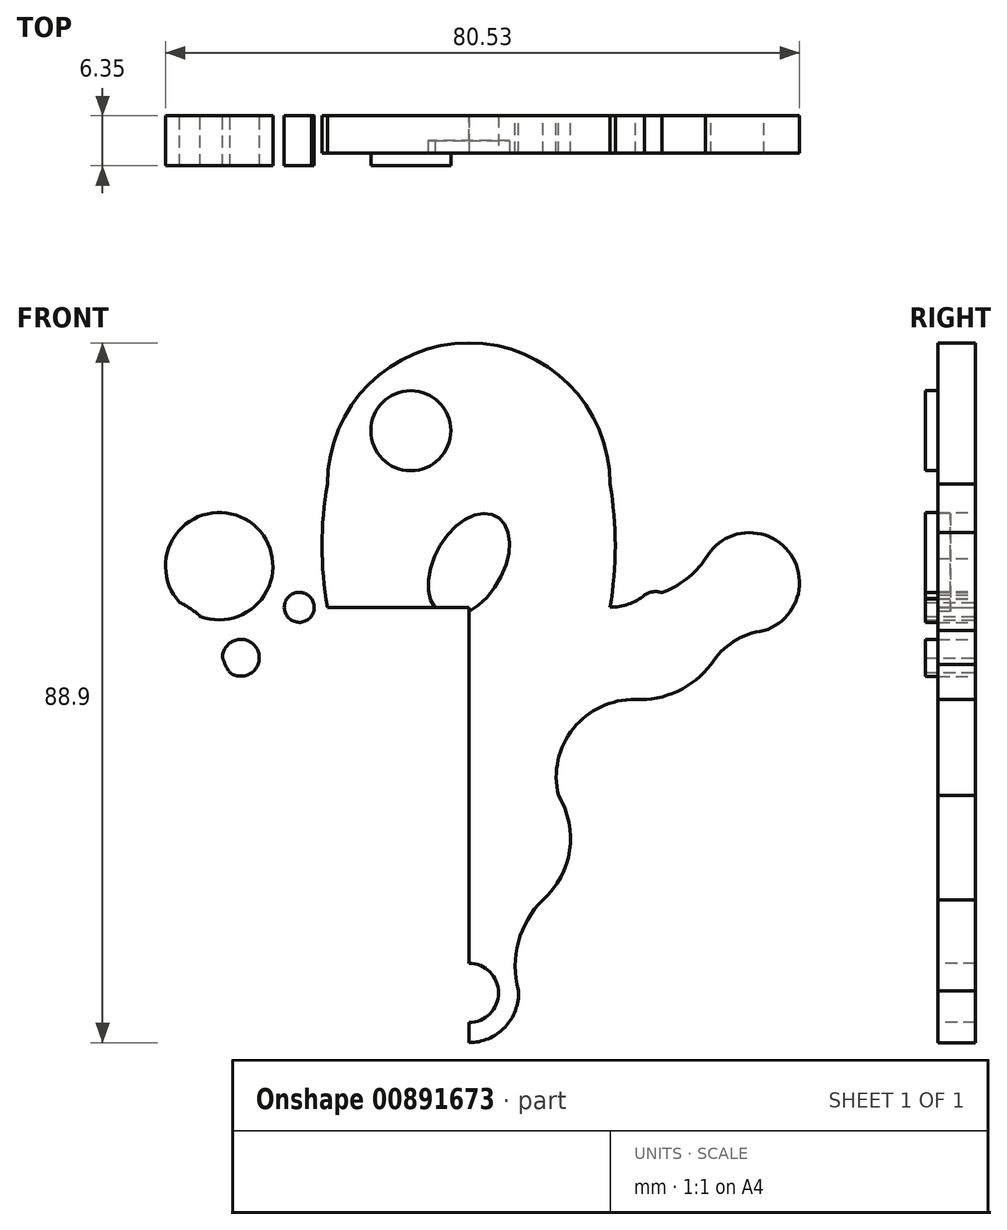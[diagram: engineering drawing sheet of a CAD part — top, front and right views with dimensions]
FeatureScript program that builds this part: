
annotation { "Feature Type Name" : "Feature", "Feature Type Description" : "" }
export const myFeature = defineFeature(function(context is Context, id is Id, definition is map)
    precondition{}
    {
        {
            var Q0;
            Q0=qCreatedBy(makeId("Front.planeOp"),FACE);
            var sketch = newSketch(context, id + "F0", { "sketchPlane" : qUnion([Q0])});
            skLineSegment(sketch, "E0.bottom", {"start": v(-17.94, 11.59) * mm, "end": v(17.94, 11.59) * mm});
            skLineSegment(sketch, "E0.top", {"start": v(-17.94, 27.23) * mm, "end": v(17.94, 27.23) * mm});
            skPoint(sketch, "E0.middle", {"position": v(0, 19.41) * mm});
            skArc(sketch, "E1", {"start": v(17.94, 27.23) * mm, "mid": v(0, 45.18) * mm, "end": v(-17.94, 27.23) * mm});
            skLineSegment(sketch, "E2", {"start": v(-17.94, 11.59) * mm, "end": v(0, 11.59) * mm});
            skLineSegment(sketch, "E3", {"start": v(0, 11.59) * mm, "end": v(0, -27.44) * mm});
            skLineSegment(sketch, "E4", {"start": v(0, -27.44) * mm, "end": v(0, -34) * mm});
            skCircle(sketch, "E5", {"center": v(-31.7, 16.82) * mm, "radius": 6.82 * mm});
            skCircle(sketch, "E6", {"center": v(35.65, 14.71) * mm, "radius": 6.36 * mm});
            skCircle(sketch, "E7", {"center": v(0, -37.4) * mm, "radius": 6.33 * mm});
            skCircle(sketch, "E8", {"center": v(-28.95, 5.17) * mm, "radius": 2.34 * mm});
            skCircle(sketch, "E9", {"center": v(-21.53, 11.59) * mm, "radius": 1.9 * mm});
            skArc(sketch, "E10", {"start": v(-19.98, 12.7) * mm, "mid": v(-19.1, 11.88) * mm, "end": v(-17.94, 11.59) * mm});
            skArc(sketch, "E11", {"start": v(-25.07, 18.4) * mm, "mid": v(-23.74, 15.74) * mm, "end": v(-21.82, 13.47) * mm});
            skArc(sketch, "E12", {"start": v(-6.2, -36.14) * mm, "mid": v(-8.21, -28.4) * mm, "end": v(-14.49, -23.44) * mm});
            skArc(sketch, "E13", {"start": v(-31.29, 5.17) * mm, "mid": v(-29.02, 1.8) * mm, "end": v(-25.38, 0) * mm});
            skPoint(sketch, "E14.startSnap0", {"position": v(10.2, -17.56) * mm});
            skArc(sketch, "E15", {"start": v(21.15, -0.12) * mm, "mid": v(13.28, -3.81) * mm, "end": v(11.38, -12.3) * mm});
            skArc(sketch, "E16", {"start": v(21.15, -0.12) * mm, "mid": v(26.51, 0.92) * mm, "end": v(30.77, 4.35) * mm});
            skCircle(sketch, "E17", {"center": v(23.71, 11.2) * mm, "radius": 2.37 * mm});
            skArc(sketch, "E18", {"start": v(24.52, 13.44) * mm, "mid": v(27.64, 15.17) * mm, "end": v(30.08, 17.78) * mm});
            skArc(sketch, "E19", {"start": v(17.94, 11.59) * mm, "mid": v(20.27, 11.99) * mm, "end": v(22.33, 13.14) * mm});
            skArc(sketch, "E20", {"start": v(37.47, 8.62) * mm, "mid": v(33.64, 7.23) * mm, "end": v(30.77, 4.35) * mm});
            skArc(sketch, "E21", {"start": v(-17.94, 27.23) * mm, "mid": v(-18.64, 19.41) * mm, "end": v(-17.94, 11.59) * mm});
            skArc(sketch, "E22", {"start": v(17.94, 11.59) * mm, "mid": v(18.6, 19.41) * mm, "end": v(17.94, 27.23) * mm});
            skArc(sketch, "E23", {"start": v(-20.49, -14.03) * mm, "mid": v(-19.15, -19.8) * mm, "end": v(-14.49, -23.44) * mm});
            skArc(sketch, "E24", {"start": v(-20.49, -14.03) * mm, "mid": v(-19.5, -5.82) * mm, "end": v(-25.38, 0) * mm});
            skArc(sketch, "E25", {"start": v(-31.29, 5.17) * mm, "mid": v(-33.14, 9.34) * mm, "end": v(-36.7, 12.19) * mm});
            skArc(sketch, "E26", {"start": v(9.44, -25.57) * mm, "mid": v(12.8, -19.28) * mm, "end": v(11.38, -12.3) * mm});
            skArc(sketch, "E27", {"start": v(9.44, -25.57) * mm, "mid": v(6.3, -30.92) * mm, "end": v(6.33, -37.12) * mm});
            skLineSegment(sketch, "E28", {"start": v(0, 45.18) * mm, "end": v(0, -43.72) * mm});
            skSolve(sketch);
        }
        {
            var Q0;
            Q0=makeQuery(id+"F0.imprint","IMPRINT",FACE,{"disambiguationData":[TD([[makeQuery(id+"F0.imprint","IMPRINT",EDGE,{"derivedFrom":sQuery(id+"F0.wireOp",EDGE,"E0.top")}),1.0]])]});
            var Q1;
            Q1=makeQuery(id+"F0.imprint","IMPRINT",FACE,{"disambiguationData":[TD([[makeQuery(id+"F0.imprint","IMPRINT",EDGE,{"derivedFrom":sQuery(id+"F0.wireOp",EDGE,"E0.bottom")}),1.0]])]});
            var Q2;
            {var subQ3=sQuery(id+"F0.wireOp",EDGE,"E2");Q2=makeQuery(id+"F0.imprint","IMPRINT",FACE,{"disambiguationData":[TD([[makeQuery(id+"F0.imprint","IMPRINT",EDGE,{"derivedFrom":subQ3}),-1.0]])]});}
            var Q3;
            {var subQ0=sQuery(id+"F0.wireOp",EDGE,"E5");var subQ1=makeQuery(id+"F0.imprint","INTERSECT",VERTEX,{"derivedFrom":[subQ0,sQuery(id+"F0.wireOp",EDGE,"E11")]});Q3=makeQuery(id+"F0.imprint","IMPRINT",FACE,{"disambiguationData":[TD([[makeQuery(id+"F0.imprint","IMPRINT",EDGE,{"disambiguationData":[TD([[subQ1,-1.0]])],"derivedFrom":subQ0}),1.0]])]});}
            var Q4;
            {var subQ12=sQuery(id+"F0.wireOp",EDGE,"E0.bottom");Q4=makeQuery(id+"F0.imprint","IMPRINT",FACE,{"disambiguationData":[TD([[makeQuery(id+"F0.imprint","IMPRINT",EDGE,{"derivedFrom":subQ12}),-1.0]])]});}
            var Q5;
            {var subQ0=sQuery(id+"F0.wireOp",EDGE,"E6");var subQ1=makeQuery(id+"F0.imprint","INTERSECT",VERTEX,{"derivedFrom":[subQ0,sQuery(id+"F0.wireOp",EDGE,"E18")]});Q5=makeQuery(id+"F0.imprint","IMPRINT",FACE,{"disambiguationData":[TD([[makeQuery(id+"F0.imprint","IMPRINT",EDGE,{"disambiguationData":[TD([[subQ1,-1.0]])],"derivedFrom":subQ0}),1.0]])]});}
            var Q6;
            {var subQ0=sQuery(id+"F0.wireOp",EDGE,"E17");var subQ1=makeQuery(id+"F0.imprint","INTERSECT",VERTEX,{"derivedFrom":[subQ0,sQuery(id+"F0.wireOp",EDGE,"E18")]});Q6=makeQuery(id+"F0.imprint","IMPRINT",FACE,{"disambiguationData":[TD([[makeQuery(id+"F0.imprint","IMPRINT",EDGE,{"disambiguationData":[TD([[subQ1,-1.0]])],"derivedFrom":subQ0}),1.0]])]});}
            var Q7;
            {var subQ0=sQuery(id+"F0.wireOp",EDGE,"E10");var subQ1=sQuery(id+"F0.wireOp",EDGE,"E9");var subQ2=makeQuery(id+"F0.imprint","INTERSECT",VERTEX,{"disambiguationData":[OD(0.0)],"derivedFrom":[subQ1,subQ0]});Q7=makeQuery(id+"F0.imprint","IMPRINT",FACE,{"disambiguationData":[TD([[makeQuery(id+"F0.imprint","IMPRINT",EDGE,{"disambiguationData":[TD([[subQ2,-1.0]])],"derivedFrom":subQ1}),1.0]])]});}
            var Q8;
            {var subQ0=sQuery(id+"F0.wireOp",EDGE,"E13");var subQ1=sQuery(id+"F0.wireOp",EDGE,"E8");var subQ3=makeQuery(id+"F0.imprint","INTERSECT",VERTEX,{"derivedFrom":[subQ1,subQ0]});Q8=makeQuery(id+"F0.imprint","IMPRINT",FACE,{"disambiguationData":[TD([[makeQuery(id+"F0.imprint","IMPRINT",EDGE,{"disambiguationData":[TD([[subQ3,-1.0]])],"derivedFrom":subQ1}),1.0]])]});}
            var Q9;
            {var subQ0=sQuery(id+"F0.wireOp",EDGE,"E7");var subQ1=makeQuery(id+"F0.imprint","INTERSECT",VERTEX,{"derivedFrom":[sQuery(id+"F0.wireOp",EDGE,"E4"),subQ0]});Q9=makeQuery(id+"F0.imprint","IMPRINT",FACE,{"disambiguationData":[TD([[makeQuery(id+"F0.imprint","IMPRINT",EDGE,{"disambiguationData":[TD([[subQ1,1.0]])],"derivedFrom":subQ0}),1.0]])]});}
            var Q10;
            {var subQ0=sQuery(id+"F0.wireOp",EDGE,"E28");var subQ1=makeQuery(id+"F0.imprint","IMPRINT",VERTEX,{"derivedFrom":subQ0});Q10=makeQuery(id+"F0.imprint","IMPRINT",FACE,{"disambiguationData":[TD([[makeQuery(id+"F0.imprint","IMPRINT",EDGE,{"disambiguationData":[TD([[subQ1,1.0]])],"derivedFrom":subQ0}),1.0]])]});}
            var Q11;
            {var subQ4=sQuery(id+"F0.wireOp",EDGE,"E2");Q11=makeQuery(id+"F0.imprint","IMPRINT",FACE,{"disambiguationData":[TD([[makeQuery(id+"F0.imprint","IMPRINT",EDGE,{"derivedFrom":subQ4}),1.0]])]});}
            extrude(context, id + "F1", {"entities" : qUnion([Q0, Q1, Q2, Q3, Q4, Q5, Q6, Q7, Q8, Q9, Q10, Q11]), "depth" : 6.35 * mm, "offsetDistance" : 25.4 * mm});
        }
        {
            var Q0;
            Q0=makeQuery(id+"F1.opExtrude","CAP_FACE",FACE,{"disambiguationData":[OSD([sQuery(id+"F0.wireOp",EDGE,"E1"),sQuery(id+"F0.wireOp",EDGE,"E5"),sQuery(id+"F0.wireOp",EDGE,"E6"),sQuery(id+"F0.wireOp",EDGE,"E7"),sQuery(id+"F0.wireOp",EDGE,"E9"),sQuery(id+"F0.wireOp",EDGE,"E10"),sQuery(id+"F0.wireOp",EDGE,"E11"),sQuery(id+"F0.wireOp",EDGE,"E12"),sQuery(id+"F0.wireOp",EDGE,"E13"),sQuery(id+"F0.wireOp",EDGE,"E15"),sQuery(id+"F0.wireOp",EDGE,"E16"),sQuery(id+"F0.wireOp",EDGE,"E17"),sQuery(id+"F0.wireOp",EDGE,"E18"),sQuery(id+"F0.wireOp",EDGE,"E19"),sQuery(id+"F0.wireOp",EDGE,"E20"),sQuery(id+"F0.wireOp",EDGE,"E21"),sQuery(id+"F0.wireOp",EDGE,"E22"),sQuery(id+"F0.wireOp",EDGE,"E23"),sQuery(id+"F0.wireOp",EDGE,"E24"),sQuery(id+"F0.wireOp",EDGE,"E25"),sQuery(id+"F0.wireOp",EDGE,"E26"),sQuery(id+"F0.wireOp",EDGE,"E27")])],"isStart":false});
            var sketch = newSketch(context, id + "F2", { "sketchPlane" : qUnion([Q0])});
            skCircle(sketch, "E29", {"center": v(7.39, 31.47) * mm, "radius": 5.22 * mm});
            skEllipse(sketch, "E30", {"center": v(0, 17.03) * mm, "majorRadius": 7.04 * mm, "minorRadius": 4.37 * mm, "majorAxis": v(-0.5, -0.87)});
            skCircle(sketch, "E31", {"center": v(-7.37, 34.04) * mm, "radius": 5.08 * mm});
            skCircle(sketch, "E32", {"center": v(0, -37.4) * mm, "radius": 3.64 * mm});
            skLineSegment(sketch, "E33", {"start": v(-7.37, 34.04) * mm, "end": v(0, 34.04) * mm});
            skLineSegment(sketch, "E34", {"start": v(7.39, 31.47) * mm, "end": v(0, 31.47) * mm});
            skPoint(sketch, "E34.endSnap0", {"position": v(0, 45.18) * mm});
            skLineSegment(sketch, "E35", {"start": v(0, 34.04) * mm, "end": v(0, 45.18) * mm});
            skLineSegment(sketch, "E36", {"start": v(0, 31.47) * mm, "end": v(0, 45.18) * mm});
            skSolve(sketch);
        }
        {
            var Q0;
            Q0=makeQuery(id+"F2.imprint","IMPRINT",FACE,{"disambiguationData":[TD([[makeQuery(id+"F2.imprint","IMPRINT",EDGE,{"derivedFrom":sQuery(id+"F2.wireOp",EDGE,"E30")}),1.0]])]});
            var Q1;
            Q1=sQuery(id+"F2.wireOp",EDGE,"E30");
            extrude(context, id + "F3", {"entities" : qUnion([Q0]), "operationType" : NewBodyOperationType.REMOVE, "surfaceEntities" : qUnion([Q1]), "oppositeDirection" : true, "depth" : 3.17 * mm, "offsetDistance" : 25.4 * mm});
        }
        {
            var Q0;
            Q0=makeQuery(id+"F1.opExtrude","CAP_FACE",FACE,{"disambiguationData":[OSD([sQuery(id+"F0.wireOp",EDGE,"E1"),sQuery(id+"F0.wireOp",EDGE,"E5"),sQuery(id+"F0.wireOp",EDGE,"E6"),sQuery(id+"F0.wireOp",EDGE,"E7"),sQuery(id+"F0.wireOp",EDGE,"E9"),sQuery(id+"F0.wireOp",EDGE,"E10"),sQuery(id+"F0.wireOp",EDGE,"E11"),sQuery(id+"F0.wireOp",EDGE,"E12"),sQuery(id+"F0.wireOp",EDGE,"E13"),sQuery(id+"F0.wireOp",EDGE,"E15"),sQuery(id+"F0.wireOp",EDGE,"E16"),sQuery(id+"F0.wireOp",EDGE,"E17"),sQuery(id+"F0.wireOp",EDGE,"E18"),sQuery(id+"F0.wireOp",EDGE,"E19"),sQuery(id+"F0.wireOp",EDGE,"E20"),sQuery(id+"F0.wireOp",EDGE,"E21"),sQuery(id+"F0.wireOp",EDGE,"E22"),sQuery(id+"F0.wireOp",EDGE,"E23"),sQuery(id+"F0.wireOp",EDGE,"E24"),sQuery(id+"F0.wireOp",EDGE,"E25"),sQuery(id+"F0.wireOp",EDGE,"E26"),sQuery(id+"F0.wireOp",EDGE,"E27")])],"isStart":false});
            var sketch = newSketch(context, id + "F4", { "sketchPlane" : qUnion([Q0])});
            skLineSegment(sketch, "E37", {"start": v(0, 45.18) * mm, "end": v(0, 34.03) * mm});
            skLineSegment(sketch, "E38", {"start": v(0, 34.03) * mm, "end": v(0, 45.18) * mm});
            skLineSegment(sketch, "E39", {"start": v(0, 45.18) * mm, "end": v(0, 31.46) * mm});
            skLineSegment(sketch, "E40", {"start": v(0, 34.03) * mm, "end": v(-7.37, 34.03) * mm});
            skLineSegment(sketch, "E41", {"start": v(0, 31.46) * mm, "end": v(7.37, 31.46) * mm});
            skCircle(sketch, "E42", {"center": v(-7.37, 34.03) * mm, "radius": 5.08 * mm});
            skCircle(sketch, "E43", {"center": v(7.37, 31.46) * mm, "radius": 5.22 * mm});
            skSolve(sketch);
        }
        {
            var Q0;
            Q0=makeQuery(id+"F4.imprint","IMPRINT",FACE,{"disambiguationData":[TD([[makeQuery(id+"F4.imprint","IMPRINT",EDGE,{"derivedFrom":sQuery(id+"F4.wireOp",EDGE,"E42")}),-1.0]])]});
            var Q1;
            Q1=makeQuery(id+"F4.imprint","IMPRINT",FACE,{"disambiguationData":[TD([[makeQuery(id+"F4.imprint","IMPRINT",EDGE,{"derivedFrom":sQuery(id+"F4.wireOp",EDGE,"E43")}),1.0]])]});
            extrude(context, id + "F5", {"entities" : qUnion([Q0, Q1]), "operationType" : NewBodyOperationType.REMOVE, "oppositeDirection" : true, "depth" : 1.59 * mm, "offsetDistance" : 25.4 * mm});
        }
        {
            var Q0;
            Q0=makeQuery(id+"F1.opExtrude","CAP_FACE",FACE,{"disambiguationData":[OSD([sQuery(id+"F0.wireOp",EDGE,"E1"),sQuery(id+"F0.wireOp",EDGE,"E5"),sQuery(id+"F0.wireOp",EDGE,"E6"),sQuery(id+"F0.wireOp",EDGE,"E7"),sQuery(id+"F0.wireOp",EDGE,"E9"),sQuery(id+"F0.wireOp",EDGE,"E10"),sQuery(id+"F0.wireOp",EDGE,"E11"),sQuery(id+"F0.wireOp",EDGE,"E12"),sQuery(id+"F0.wireOp",EDGE,"E13"),sQuery(id+"F0.wireOp",EDGE,"E15"),sQuery(id+"F0.wireOp",EDGE,"E16"),sQuery(id+"F0.wireOp",EDGE,"E17"),sQuery(id+"F0.wireOp",EDGE,"E18"),sQuery(id+"F0.wireOp",EDGE,"E19"),sQuery(id+"F0.wireOp",EDGE,"E20"),sQuery(id+"F0.wireOp",EDGE,"E21"),sQuery(id+"F0.wireOp",EDGE,"E22"),sQuery(id+"F0.wireOp",EDGE,"E23"),sQuery(id+"F0.wireOp",EDGE,"E24"),sQuery(id+"F0.wireOp",EDGE,"E25"),sQuery(id+"F0.wireOp",EDGE,"E26"),sQuery(id+"F0.wireOp",EDGE,"E27")])],"isStart":false});
            var sketch = newSketch(context, id + "F6", { "sketchPlane" : qUnion([Q0])});
            skCircle(sketch, "E44", {"center": v(0, -37.4) * mm, "radius": 3.77 * mm});
            skSolve(sketch);
        }
        {
            var Q0;
            Q0=makeQuery(id+"F6.imprint","IMPRINT",FACE,{"disambiguationData":[TD([[makeQuery(id+"F6.imprint","IMPRINT",EDGE,{"derivedFrom":sQuery(id+"F6.wireOp",EDGE,"E44")}),1.0]])]});
            extrude(context, id + "F7", {"entities" : qUnion([Q0]), "operationType" : NewBodyOperationType.REMOVE, "oppositeDirection" : true, "depth" : 25.4 * mm, "offsetDistance" : 25.4 * mm});
        }
        {
            var Q0;
            Q0=makeQuery(id+"F1.opExtrude","CAP_FACE",FACE,{"disambiguationData":[OSD([sQuery(id+"F0.wireOp",EDGE,"E1"),sQuery(id+"F0.wireOp",EDGE,"E5"),sQuery(id+"F0.wireOp",EDGE,"E6"),sQuery(id+"F0.wireOp",EDGE,"E7"),sQuery(id+"F0.wireOp",EDGE,"E9"),sQuery(id+"F0.wireOp",EDGE,"E10"),sQuery(id+"F0.wireOp",EDGE,"E11"),sQuery(id+"F0.wireOp",EDGE,"E12"),sQuery(id+"F0.wireOp",EDGE,"E13"),sQuery(id+"F0.wireOp",EDGE,"E15"),sQuery(id+"F0.wireOp",EDGE,"E16"),sQuery(id+"F0.wireOp",EDGE,"E17"),sQuery(id+"F0.wireOp",EDGE,"E18"),sQuery(id+"F0.wireOp",EDGE,"E19"),sQuery(id+"F0.wireOp",EDGE,"E20"),sQuery(id+"F0.wireOp",EDGE,"E21"),sQuery(id+"F0.wireOp",EDGE,"E22"),sQuery(id+"F0.wireOp",EDGE,"E23"),sQuery(id+"F0.wireOp",EDGE,"E24"),sQuery(id+"F0.wireOp",EDGE,"E25"),sQuery(id+"F0.wireOp",EDGE,"E26"),sQuery(id+"F0.wireOp",EDGE,"E27")])],"isStart":false});
            var sketch = newSketch(context, id + "F8", { "sketchPlane" : qUnion([Q0])});
            skPoint(sketch, "E45.secondSnap0", {"position": v(13.28, -3.81) * mm});
            skText(sketch, "E46", { "text": "      The \n      ISS\'s\n    Friendly \n Space Ghost", "fontName": "AllertaStencil-Regular.ttf"});
            const initialGuessF8  = {"E46": [-0.01736, 0, 1, 0, 0.00316]};
            skSetInitialGuess(sketch, initialGuessF8);
            skSolve(sketch);
        }
        {
            var Q0;
            Q0 = qSketchRegion(id + "F8", true);
            extrude(context, id + "F9", {"entities" : qUnion([Q0]), "operationType" : NewBodyOperationType.REMOVE, "oppositeDirection" : true, "depth" : 1.27 * mm, "offsetDistance" : 25.4 * mm});
        }
    });
